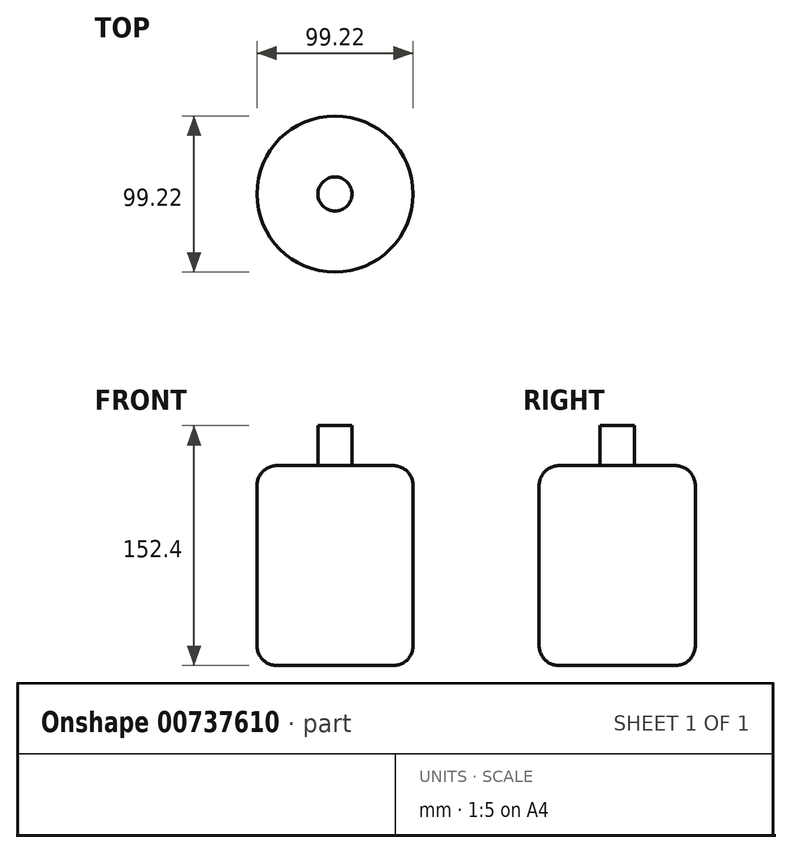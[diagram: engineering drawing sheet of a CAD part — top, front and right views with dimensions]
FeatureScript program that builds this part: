
annotation { "Feature Type Name" : "Feature", "Feature Type Description" : "" }
export const myFeature = defineFeature(function(context is Context, id is Id, definition is map)
    precondition{}
    {
        {
            var Q0;
            Q0=qCreatedBy(makeId("Top.planeOp"),FACE);
            var sketch = newSketch(context, id + "F0", { "sketchPlane" : qUnion([Q0])});
            skCircle(sketch, "E0", {"center": v(0, 0) * mm, "radius": 49.6 * mm});
            skSolve(sketch);
        }
        {
            var Q0;
            Q0 = qSketchRegion(id + "F0", true);
            extrude(context, id + "F1", {"entities" : qUnion([Q0]), "depth" : 127 * mm, "offsetDistance" : 25.4 * mm});
        }
        {
            var Q0;
            Q0=makeQuery(id+"F1.opExtrude","CAP_FACE",FACE,{"disambiguationData":[OSD([sQuery(id+"F0.wireOp",EDGE,"E0")])],"isStart":false});
            var sketch = newSketch(context, id + "F2", { "sketchPlane" : qUnion([Q0])});
            skCircle(sketch, "E1", {"center": v(0, 0) * mm, "radius": 10.85 * mm});
            skSolve(sketch);
        }
        {
            var Q0;
            Q0 = qSketchRegion(id + "F2", true);
            extrude(context, id + "F3", {"entities" : qUnion([Q0]), "operationType" : NewBodyOperationType.ADD, "depth" : 25.4 * mm, "offsetDistance" : 25.4 * mm});
        }
        {
            var Q0;
            Q0=makeQuery(id+"F1.opExtrude","CAP_EDGE",EDGE,{"disambiguationData":[OSD([sQuery(id+"F0.wireOp",EDGE,"E0")])],"isStart":false});
            var Q1;
            Q1=makeQuery(id+"F1.opExtrude","SWEPT_FACE",FACE,{"disambiguationData":[OSD([sQuery(id+"F0.wireOp",EDGE,"E0")])]});
            fillet(context, id + "F4", {"entities" : qUnion([Q0, Q1]), "radius" : 12.7 * mm, "tangentPropagation" : true, "allowEdgeOverflow" : false});
        }
    });
